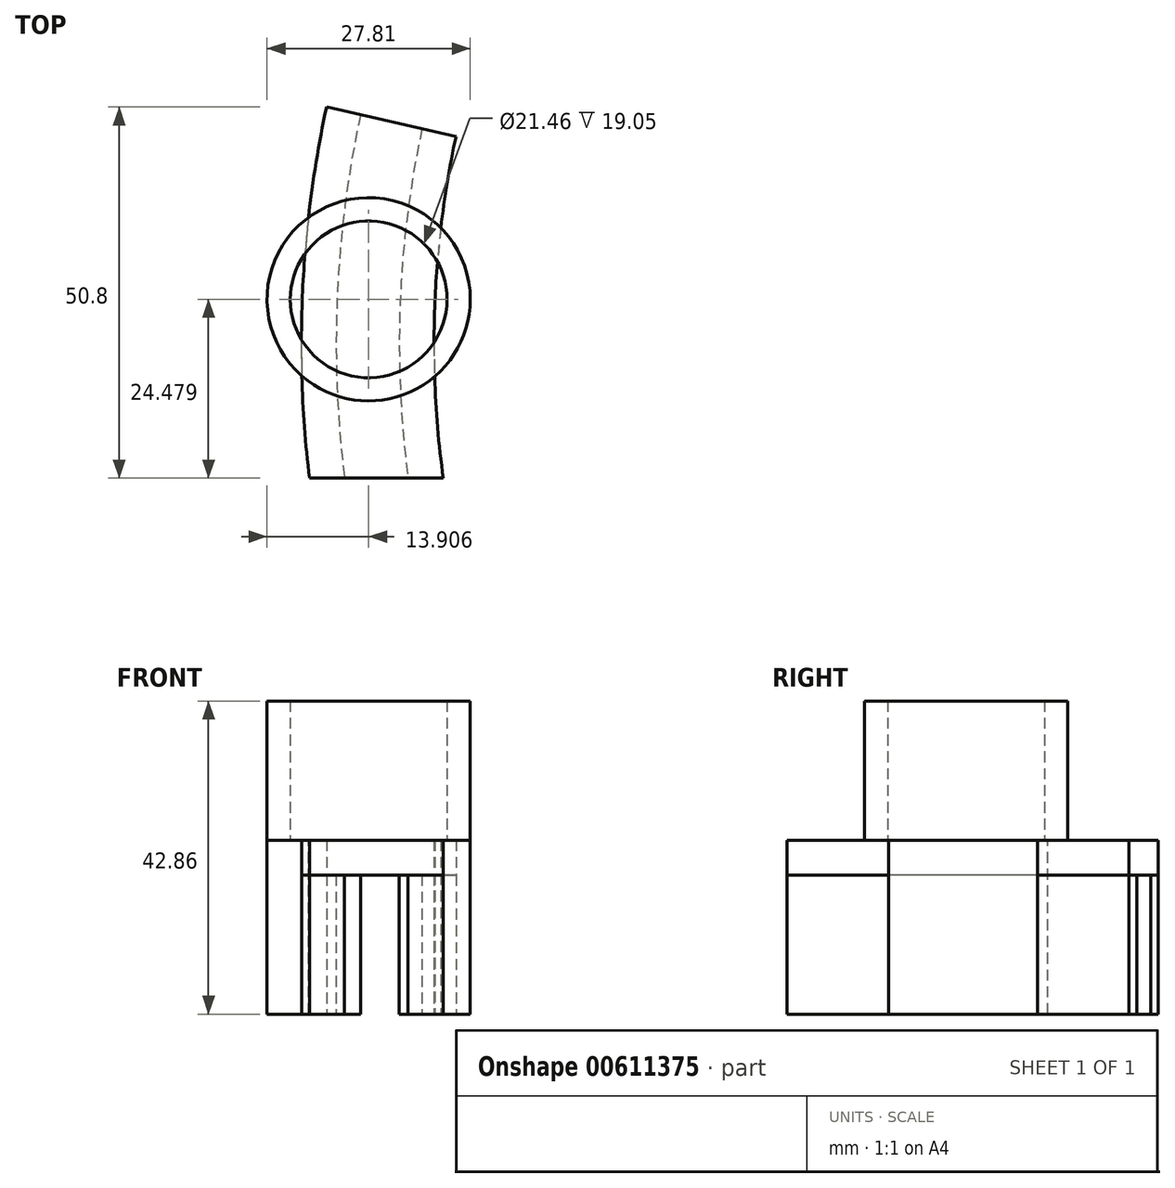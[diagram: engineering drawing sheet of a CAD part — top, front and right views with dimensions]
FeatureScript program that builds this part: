
annotation { "Feature Type Name" : "Feature", "Feature Type Description" : "" }
export const myFeature = defineFeature(function(context is Context, id is Id, definition is map)
    precondition{}
    {
        {
            var Q0;
            Q0=qCreatedBy(makeId("Top.planeOp"),FACE);
            var sketch = newSketch(context, id + "F0", { "sketchPlane" : qUnion([Q0])});
            skCircle(sketch, "E0", {"center": v(0, 0) * mm, "radius": 140.5 * mm});
            skCircle(sketch, "E1.0", {"center": v(0, 0) * mm, "radius": 149.13 * mm});
            skCircle(sketch, "E2.0", {"center": v(0, 0) * mm, "radius": 135.73 * mm});
            skCircle(sketch, "E3.0", {"center": v(0, 0) * mm, "radius": 153.9 * mm});
            skLineSegment(sketch, "E4", {"start": v(-150.45, 32.38) * mm, "end": v(-132.73, 28.36) * mm});
            skLineSegment(sketch, "E5", {"start": v(-152.79, -18.42) * mm, "end": v(-134.47, -18.42) * mm});
            skSolve(sketch);
        }
        {
            var Q0;
            {var subQ0=sQuery(id+"F0.wireOp",EDGE,"E4");var subQ1=sQuery(id+"F0.wireOp",EDGE,"E0");var subQ2=makeQuery(id+"F0.imprint","INTERSECT",VERTEX,{"derivedFrom":[subQ1,subQ0]});Q0=makeQuery(id+"F0.imprint","IMPRINT",FACE,{"disambiguationData":[TD([[makeQuery(id+"F0.imprint","IMPRINT",EDGE,{"disambiguationData":[TD([[subQ2,-1.0]])],"derivedFrom":subQ1}),1.0]])]});}
            var Q1;
            {var subQ0=sQuery(id+"F0.wireOp",EDGE,"E4");var subQ1=sQuery(id+"F0.wireOp",EDGE,"E1.0");var subQ2=makeQuery(id+"F0.imprint","INTERSECT",VERTEX,{"derivedFrom":[subQ1,subQ0]});Q1=makeQuery(id+"F0.imprint","IMPRINT",FACE,{"disambiguationData":[TD([[makeQuery(id+"F0.imprint","IMPRINT",EDGE,{"disambiguationData":[TD([[subQ2,-1.0]])],"derivedFrom":subQ1}),-1.0]])]});}
            extrude(context, id + "F1", {"entities" : qUnion([Q0, Q1]), "depth" : 19.05 * mm, "offsetDistance" : 25.4 * mm});
        }
        {
            var Q0;
            Q0=makeQuery(id+"F1.opExtrude","CAP_FACE",FACE,{"disambiguationData":[OSD([sQuery(id+"F0.wireOp",EDGE,"E1.0"),sQuery(id+"F0.wireOp",EDGE,"E3.0"),sQuery(id+"F0.wireOp",EDGE,"E4"),sQuery(id+"F0.wireOp",EDGE,"E5")])],"isStart":false});
            var sketch = newSketch(context, id + "F2", { "sketchPlane" : qUnion([Q0])});
            skLineSegment(sketch, "E6.0", {"start": v(-150.45, 32.38) * mm, "end": v(-132.73, 28.36) * mm});
            skCircle(sketch, "E6.1", {"center": v(0, 0) * mm, "radius": 153.9 * mm});
            skLineSegment(sketch, "E6.2", {"start": v(-152.79, -18.42) * mm, "end": v(-134.47, -18.42) * mm});
            skCircle(sketch, "E6.3", {"center": v(0, 0) * mm, "radius": 135.73 * mm});
            skSolve(sketch);
        }
        {
            var Q0;
            {var subQ1=makeQuery(id+"F1.opExtrude","CAP_EDGE",EDGE,{"disambiguationData":[OSD([sQuery(id+"F0.wireOp",EDGE,"E1.0")])],"isStart":false});Q0=makeQuery(id+"F2.imprint","IMPRINT",FACE,{"disambiguationData":[TD([[makeQuery(id+"F2.imprint","IMPRINT",EDGE,{"derivedFrom":subQ1}),1.0]])]});}
            var Q1;
            {var subQ3=makeQuery(id+"F1.opExtrude","CAP_EDGE",EDGE,{"disambiguationData":[OSD([sQuery(id+"F0.wireOp",EDGE,"E1.0")])],"isStart":false});Q1=makeQuery(id+"F2.imprint","IMPRINT",FACE,{"disambiguationData":[TD([[makeQuery(id+"F2.imprint","IMPRINT",EDGE,{"derivedFrom":subQ3}),-1.0]])]});}
            extrude(context, id + "F3", {"entities" : qUnion([Q0, Q1]), "depth" : 4.76 * mm, "offsetDistance" : 25.4 * mm});
        }
        {
            var Q0;
            Q0=makeQuery(id+"F3.opExtrude","CAP_FACE",FACE,{"disambiguationData":[OSD([sQuery(id+"F2.wireOp",EDGE,"E6.0"),sQuery(id+"F2.wireOp",EDGE,"E6.1"),sQuery(id+"F2.wireOp",EDGE,"E6.2"),sQuery(id+"F2.wireOp",EDGE,"E6.3")])],"isStart":false});
            var sketch = newSketch(context, id + "F4", { "sketchPlane" : qUnion([Q0])});
            skLineSegment(sketch, "E7", {"start": v(-153.73, 7.07) * mm, "end": v(-135.64, 5.04) * mm, "construction": true});
            skPoint(sketch, "E8", {"position": v(-144.68, 6.06) * mm});
            skCircle(sketch, "E9", {"center": v(-144.68, 6.06) * mm, "radius": 10.73 * mm});
            skArc(sketch, "E10.0", {"start": v(-150.45, 32.38) * mm, "mid": v(-153.73, 7.07) * mm, "end": v(-152.79, -18.42) * mm});
            skArc(sketch, "E10.1", {"start": v(-132.73, 28.36) * mm, "mid": v(-135.64, 5.04) * mm, "end": v(-134.47, -18.42) * mm});
            skCircle(sketch, "E11.0", {"center": v(-144.68, 6.06) * mm, "radius": 13.9 * mm});
            skSolve(sketch);
        }
        {
            var Q0;
            {var subQ0=sQuery(id+"F4.wireOp",EDGE,"E10.0");var subQ1=sQuery(id+"F4.wireOp",EDGE,"E9");var subQ2=makeQuery(id+"F4.imprint","INTERSECT",VERTEX,{"disambiguationData":[OD(0.0)],"derivedFrom":[subQ1,subQ0]});Q0=makeQuery(id+"F4.imprint","IMPRINT",FACE,{"disambiguationData":[TD([[makeQuery(id+"F4.imprint","IMPRINT",EDGE,{"disambiguationData":[TD([[subQ2,-1.0]])],"derivedFrom":subQ1}),-1.0]])]});}
            var Q1;
            {var subQ0=sQuery(id+"F4.wireOp",EDGE,"E10.0");var subQ1=sQuery(id+"F4.wireOp",EDGE,"E9");var subQ2=makeQuery(id+"F4.imprint","INTERSECT",VERTEX,{"disambiguationData":[OD(0.0)],"derivedFrom":[subQ1,subQ0]});Q1=makeQuery(id+"F4.imprint","IMPRINT",FACE,{"disambiguationData":[TD([[makeQuery(id+"F4.imprint","IMPRINT",EDGE,{"disambiguationData":[TD([[subQ2,1.0]])],"derivedFrom":subQ1}),-1.0]])]});}
            var Q2;
            {var subQ0=sQuery(id+"F4.wireOp",EDGE,"E10.1");var subQ1=sQuery(id+"F4.wireOp",EDGE,"E9");var subQ2=makeQuery(id+"F4.imprint","INTERSECT",VERTEX,{"disambiguationData":[OD(0.0)],"derivedFrom":[subQ1,subQ0]});Q2=makeQuery(id+"F4.imprint","IMPRINT",FACE,{"disambiguationData":[TD([[makeQuery(id+"F4.imprint","IMPRINT",EDGE,{"disambiguationData":[TD([[subQ2,1.0]])],"derivedFrom":subQ1}),-1.0]])]});}
            var Q3;
            {var subQ0=sQuery(id+"F4.wireOp",EDGE,"E10.0");var subQ1=sQuery(id+"F4.wireOp",EDGE,"E9");var subQ2=makeQuery(id+"F4.imprint","INTERSECT",VERTEX,{"disambiguationData":[OD(1.0)],"derivedFrom":[subQ1,subQ0]});Q3=makeQuery(id+"F4.imprint","IMPRINT",FACE,{"disambiguationData":[TD([[makeQuery(id+"F4.imprint","IMPRINT",EDGE,{"disambiguationData":[TD([[subQ2,-1.0]])],"derivedFrom":subQ1}),-1.0]])]});}
            extrude(context, id + "F5", {"entities" : qUnion([Q0, Q1, Q2, Q3]), "operationType" : NewBodyOperationType.ADD, "depth" : 19.05 * mm, "offsetDistance" : 25.4 * mm});
        }
        {
            var Q0;
            {var subQ0=sQuery(id+"F4.wireOp",EDGE,"E10.0");var subQ1=sQuery(id+"F4.wireOp",EDGE,"E9");var subQ2=makeQuery(id+"F4.imprint","INTERSECT",VERTEX,{"disambiguationData":[OD(0.0)],"derivedFrom":[subQ1,subQ0]});Q0=makeQuery(id+"F4.imprint","IMPRINT",FACE,{"disambiguationData":[TD([[makeQuery(id+"F4.imprint","IMPRINT",EDGE,{"disambiguationData":[TD([[subQ2,-1.0]])],"derivedFrom":subQ1}),1.0]])]});}
            var Q1;
            {var subQ0=sQuery(id+"F4.wireOp",EDGE,"E10.0");var subQ1=sQuery(id+"F4.wireOp",EDGE,"E9");var subQ2=makeQuery(id+"F4.imprint","INTERSECT",VERTEX,{"disambiguationData":[OD(0.0)],"derivedFrom":[subQ1,subQ0]});Q1=makeQuery(id+"F4.imprint","IMPRINT",FACE,{"disambiguationData":[TD([[makeQuery(id+"F4.imprint","IMPRINT",EDGE,{"disambiguationData":[TD([[subQ2,-1.0]])],"derivedFrom":subQ1}),-1.0]])]});}
            var Q2;
            Q2=makeQuery(id+"F1.opExtrude","CAP_FACE",FACE,{"disambiguationData":[OSD([sQuery(id+"F0.wireOp",EDGE,"E1.0"),sQuery(id+"F0.wireOp",EDGE,"E3.0"),sQuery(id+"F0.wireOp",EDGE,"E4"),sQuery(id+"F0.wireOp",EDGE,"E5")])],"isStart":true});
            extrude(context, id + "F6", {"entities" : qUnion([Q0, Q1]), "endBound" : BoundingType.UP_TO_SURFACE, "oppositeDirection" : true, "depth" : 25.4 * mm, "endBoundEntityFace" : qUnion([Q2]), "offsetDistance" : 25.4 * mm});
        }
        {
            var Q0;
            {var subQ0=sQuery(id+"F0.wireOp",EDGE,"E2.0");var subQ1=makeQuery(id+"F0.imprint","INTERSECT",VERTEX,{"derivedFrom":[subQ0,sQuery(id+"F0.wireOp",EDGE,"E4")]});Q0=makeQuery(id+"F0.imprint","IMPRINT",FACE,{"disambiguationData":[TD([[makeQuery(id+"F0.imprint","IMPRINT",EDGE,{"disambiguationData":[TD([[subQ1,-1.0]])],"derivedFrom":subQ0}),1.0]])]});}
            var sketch = newSketch(context, id + "F7", { "sketchPlane" : qUnion([Q0])});
            skArc(sketch, "E12.0", {"start": v(-132.73, 28.36) * mm, "mid": v(-135.64, 5.04) * mm, "end": v(-134.47, -18.42) * mm});
            skCircle(sketch, "E12.1", {"center": v(-144.68, 6.06) * mm, "radius": 13.9 * mm});
            skSolve(sketch);
        }
        {
            var Q0;
            {var subQ0=sQuery(id+"F7.wireOp",EDGE,"E12.1");var subQ1=sQuery(id+"F7.wireOp",EDGE,"E12.0");var subQ2=makeQuery(id+"F7.imprint","INTERSECT",VERTEX,{"disambiguationData":[OD(0.0)],"derivedFrom":[subQ1,subQ0]});Q0=makeQuery(id+"F7.imprint","IMPRINT",FACE,{"disambiguationData":[TD([[makeQuery(id+"F7.imprint","IMPRINT",EDGE,{"disambiguationData":[TD([[subQ2,-1.0]])],"derivedFrom":subQ1}),1.0]])]});}
            var Q1;
            {var subQ0=sQuery(id+"F2.wireOp",EDGE,"E6.3");var subQ1=sQuery(id+"F4.wireOp",EDGE,"E9");var subQ2=sQuery(id+"F4.wireOp",EDGE,"E11.0");Q1=makeQuery(id+"F5.boolean.opBoolean","SPLIT",FACE,{"disambiguationData":[TD([makeQuery(id+"F3.opExtrude","SWEPT_FACE",FACE,{"disambiguationData":[OSD([subQ0])]})])],"derivedFrom":makeQuery(id+"F5.opExtrude","CAP_FACE",FACE,{"disambiguationData":[OSD([subQ1,subQ2])],"isStart":true})});}
            extrude(context, id + "F8", {"entities" : qUnion([Q0]), "endBound" : BoundingType.UP_TO_SURFACE, "depth" : 19.56 * mm, "endBoundEntityFace" : qUnion([Q1]), "offsetDistance" : 25.4 * mm});
        }
    });
